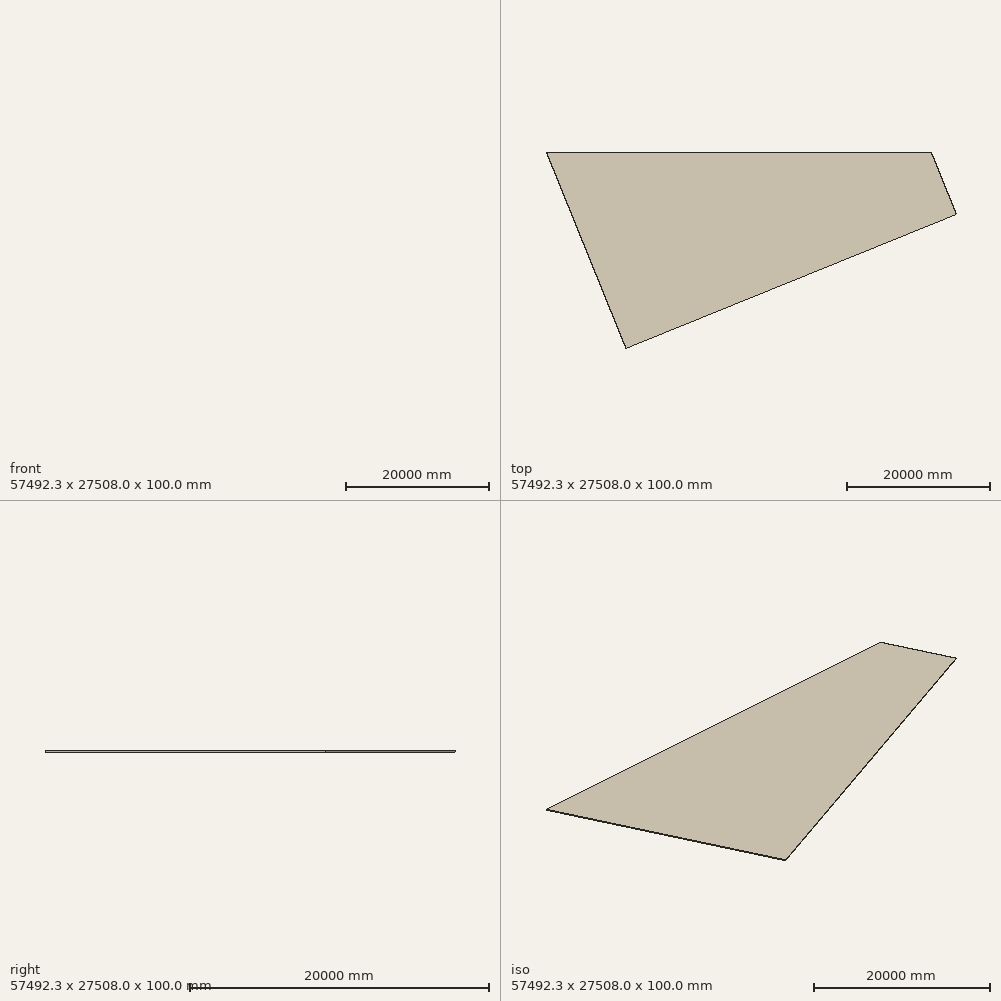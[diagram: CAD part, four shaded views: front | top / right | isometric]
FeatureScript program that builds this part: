
annotation { "Feature Type Name" : "Feature", "Feature Type Description" : "" }
export const myFeature = defineFeature(function(context is Context, id is Id, definition is map)
    precondition{}
    {
        {
            var Q0;
            Q0=qCreatedBy(makeId("Top.planeOp"),FACE);
            var sketch = newSketch(context, id + "F0", { "sketchPlane" : qUnion([Q0])});
            skLineSegment(sketch, "E0", {"start": v(-17637.46, 9453.56) * mm, "end": v(23464.36, 9453.56) * mm});
            skLineSegment(sketch, "E1", {"start": v(23464.36, 9453.56) * mm, "end": v(26998.3, 743.15) * mm});
            skLineSegment(sketch, "E2", {"start": v(26998.3, 743.15) * mm, "end": v(-19333.68, -18054.4) * mm});
            skLineSegment(sketch, "E3", {"start": v(-19333.68, -18054.4) * mm, "end": v(-30494.05, 9453.56) * mm});
            skLineSegment(sketch, "E4", {"start": v(-30494.05, 9453.56) * mm, "end": v(-17637.46, 9453.56) * mm});
            skLineSegment(sketch, "E5", {"start": v(26998.3, 743.15) * mm, "end": v(25419.3, 4635.03) * mm});
            skLineSegment(sketch, "E6", {"start": v(25419.3, 4635.03) * mm, "end": v(11519.7, -1004.23) * mm});
            skLineSegment(sketch, "E7", {"start": v(11519.7, -1004.23) * mm, "end": v(13098.7, -4896.12) * mm});
            skLineSegment(sketch, "E8", {"start": v(13098.7, -4896.12) * mm, "end": v(10782.1, -5836) * mm});
            skLineSegment(sketch, "E9", {"start": v(10782.1, -5836) * mm, "end": v(9203.11, -1944.1) * mm});
            skLineSegment(sketch, "E10", {"start": v(9203.11, -1944.1) * mm, "end": v(-4696.48, -7583.37) * mm});
            skLineSegment(sketch, "E11", {"start": v(-4696.48, -7583.37) * mm, "end": v(-3117.49, -11475.26) * mm});
            skLineSegment(sketch, "E12", {"start": v(-3117.49, -11475.26) * mm, "end": v(-5434.09, -12415.14) * mm});
            skLineSegment(sketch, "E13", {"start": v(-5434.09, -12415.14) * mm, "end": v(-7013.08, -8523.25) * mm});
            skLineSegment(sketch, "E14", {"start": v(-7013.08, -8523.25) * mm, "end": v(-20912.68, -14162.51) * mm});
            skLineSegment(sketch, "E15", {"start": v(-20912.68, -14162.51) * mm, "end": v(-19333.68, -18054.4) * mm});
            skLineSegment(sketch, "E16", {"start": v(9203.11, -1944.1) * mm, "end": v(4578.91, 9453.56) * mm});
            skPoint(sketch, "E16.endSnap0", {"position": v(2913.45, 9453.56) * mm});
            skLineSegment(sketch, "E17", {"start": v(-4696.48, -7583.37) * mm, "end": v(-11608.6, 9453.56) * mm});
            skLineSegment(sketch, "E18", {"start": v(-30494.05, 9453.56) * mm, "end": v(-30412.91, 9253.56) * mm});
            skLineSegment(sketch, "E19", {"start": v(-30412.91, 9253.56) * mm, "end": v(23545.5, 9253.56) * mm});
            skLineSegment(sketch, "E20", {"start": v(23545.5, 9253.56) * mm, "end": v(23464.36, 9453.56) * mm});
            skLineSegment(sketch, "E21", {"start": v(-30412.91, 9253.56) * mm, "end": v(-30494.05, 9453.56) * mm});
            skLineSegment(sketch, "E22", {"start": v(23464.36, 9453.56) * mm, "end": v(23545.5, 9253.56) * mm});
            skSolve(sketch);
        }
        {
            var Q0;
            Q0 = qSketchRegion(id + "F0", true);
            var Q1;
            {var subQ0=sQuery(id+"F0.wireOp",EDGE,"E10");Q1=makeQuery(id+"F0.imprint","IMPRINT",FACE,{"disambiguationData":[TD([[makeQuery(id+"F0.imprint","IMPRINT",EDGE,{"derivedFrom":subQ0}),-1.0]])]});}
            extrude(context, id + "F1", {"entities" : qUnion([Q0, Q1]), "depth" : 100 * mm, "offsetDistance" : 25 * mm});
        }
    });
